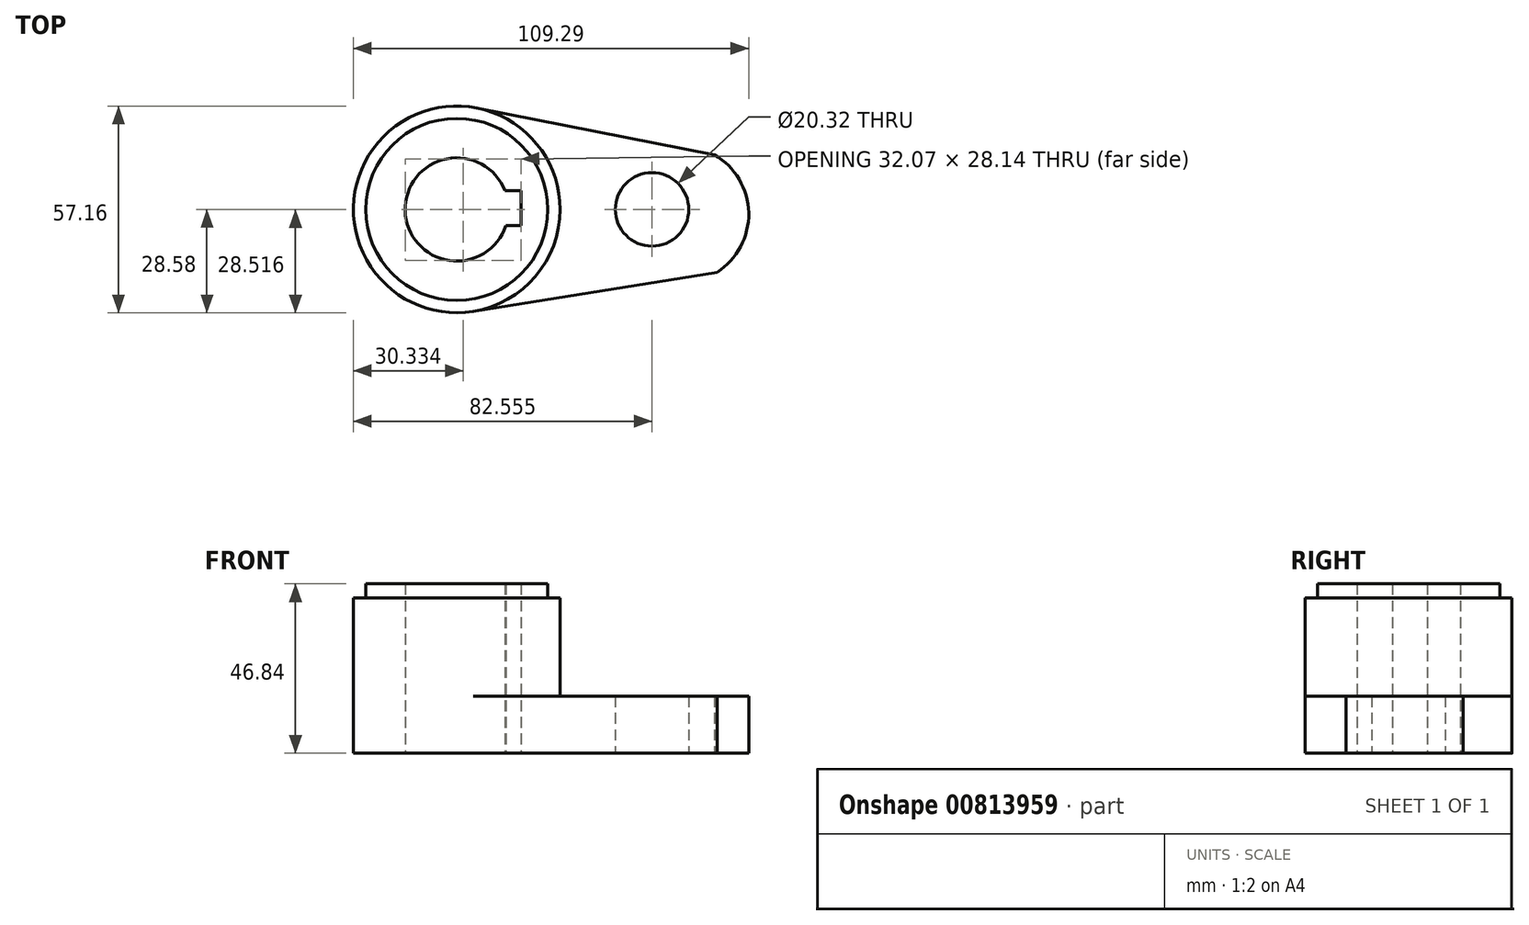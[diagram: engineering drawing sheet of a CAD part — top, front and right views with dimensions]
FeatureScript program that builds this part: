
annotation { "Feature Type Name" : "Feature", "Feature Type Description" : "" }
export const myFeature = defineFeature(function(context is Context, id is Id, definition is map)
    precondition{}
    {
        {
            var Q0;
            Q0=qCreatedBy(makeId("Top.planeOp"),FACE);
            var sketch = newSketch(context, id + "F0", { "sketchPlane" : qUnion([Q0])});
            skArc(sketch, "E0", {"start": v(13.32, 5.18) * mm, "mid": v(-14.28, -0.37) * mm, "end": v(13.57, -4.48) * mm});
            skLineSegment(sketch, "E1", {"start": v(13.32, 5.18) * mm, "end": v(17.8, 5.18) * mm});
            skLineSegment(sketch, "E2", {"start": v(17.8, 5.18) * mm, "end": v(17.8, -4.48) * mm});
            skLineSegment(sketch, "E3", {"start": v(17.8, -4.48) * mm, "end": v(13.57, -4.48) * mm});
            skCircle(sketch, "E4", {"center": v(0, 0) * mm, "radius": 28.58 * mm});
            skCircle(sketch, "E5", {"center": v(0, 0) * mm, "radius": 25.19 * mm});
            skLineSegment(sketch, "E6", {"start": v(0, 0) * mm, "end": v(53.98, 0) * mm});
            skCircle(sketch, "E7", {"center": v(53.98, 0) * mm, "radius": 10.16 * mm});
            skPoint(sketch, "E8.orphan", {"position": v(0, -28.58) * mm});
            skPoint(sketch, "E9.orphan", {"position": v(0, 28.58) * mm});
            skLineSegment(sketch, "E10", {"start": v(5.51, 28.04) * mm, "end": v(71.25, 15.11) * mm});
            skLineSegment(sketch, "E11", {"start": v(4.53, -28.21) * mm, "end": v(71.96, -17.38) * mm});
            skArc(sketch, "E12", {"start": v(71.96, -17.38) * mm, "mid": v(80.7, -0.94) * mm, "end": v(71.25, 15.11) * mm});
            skSolve(sketch);
        }
        {
            var Q0;
            Q0=makeQuery(id+"F0.imprint","IMPRINT",FACE,{"disambiguationData":[TD([[makeQuery(id+"F0.imprint","IMPRINT",EDGE,{"derivedFrom":sQuery(id+"F0.wireOp",EDGE,"E7")}),-1.0]])]});
            extrude(context, id + "F1", {"entities" : qUnion([Q0]), "depth" : 15.77 * mm, "offsetDistance" : 25.4 * mm});
        }
        {
            var Q0;
            Q0=makeQuery(id+"F0.imprint","IMPRINT",FACE,{"disambiguationData":[TD([[makeQuery(id+"F0.imprint","IMPRINT",EDGE,{"derivedFrom":sQuery(id+"F0.wireOp",EDGE,"E5")}),-1.0]])]});
            var Q1;
            Q1=makeQuery(id+"F0.imprint","IMPRINT",FACE,{"disambiguationData":[TD([[makeQuery(id+"F0.imprint","IMPRINT",EDGE,{"derivedFrom":sQuery(id+"F0.wireOp",EDGE,"E0")}),-1.0]])]});
            extrude(context, id + "F2", {"entities" : qUnion([Q0, Q1]), "operationType" : NewBodyOperationType.ADD, "depth" : 40.23 * mm, "offsetDistance" : 25.4 * mm});
        }
        {
            var Q0;
            Q0=makeQuery(id+"F0.imprint","IMPRINT",FACE,{"disambiguationData":[TD([[makeQuery(id+"F0.imprint","IMPRINT",EDGE,{"derivedFrom":sQuery(id+"F0.wireOp",EDGE,"E5")}),-1.0]])]});
            extrude(context, id + "F3", {"entities" : qUnion([Q0]), "operationType" : NewBodyOperationType.ADD, "depth" : 42.93 * mm, "offsetDistance" : 25.4 * mm});
        }
        {
            var Q0;
            Q0=makeQuery(id+"F2.opExtrude","CAP_FACE",FACE,{"disambiguationData":[OSD([sQuery(id+"F0.wireOp",EDGE,"E0"),sQuery(id+"F0.wireOp",EDGE,"E1"),sQuery(id+"F0.wireOp",EDGE,"E2"),sQuery(id+"F0.wireOp",EDGE,"E3"),sQuery(id+"F0.wireOp",EDGE,"E4")])],"isStart":false});
            extrude(context, id + "F4", {"entities" : qUnion([Q0]), "operationType" : NewBodyOperationType.ADD, "depth" : 6.6 * mm, "offsetDistance" : 25.4 * mm});
        }
    });
